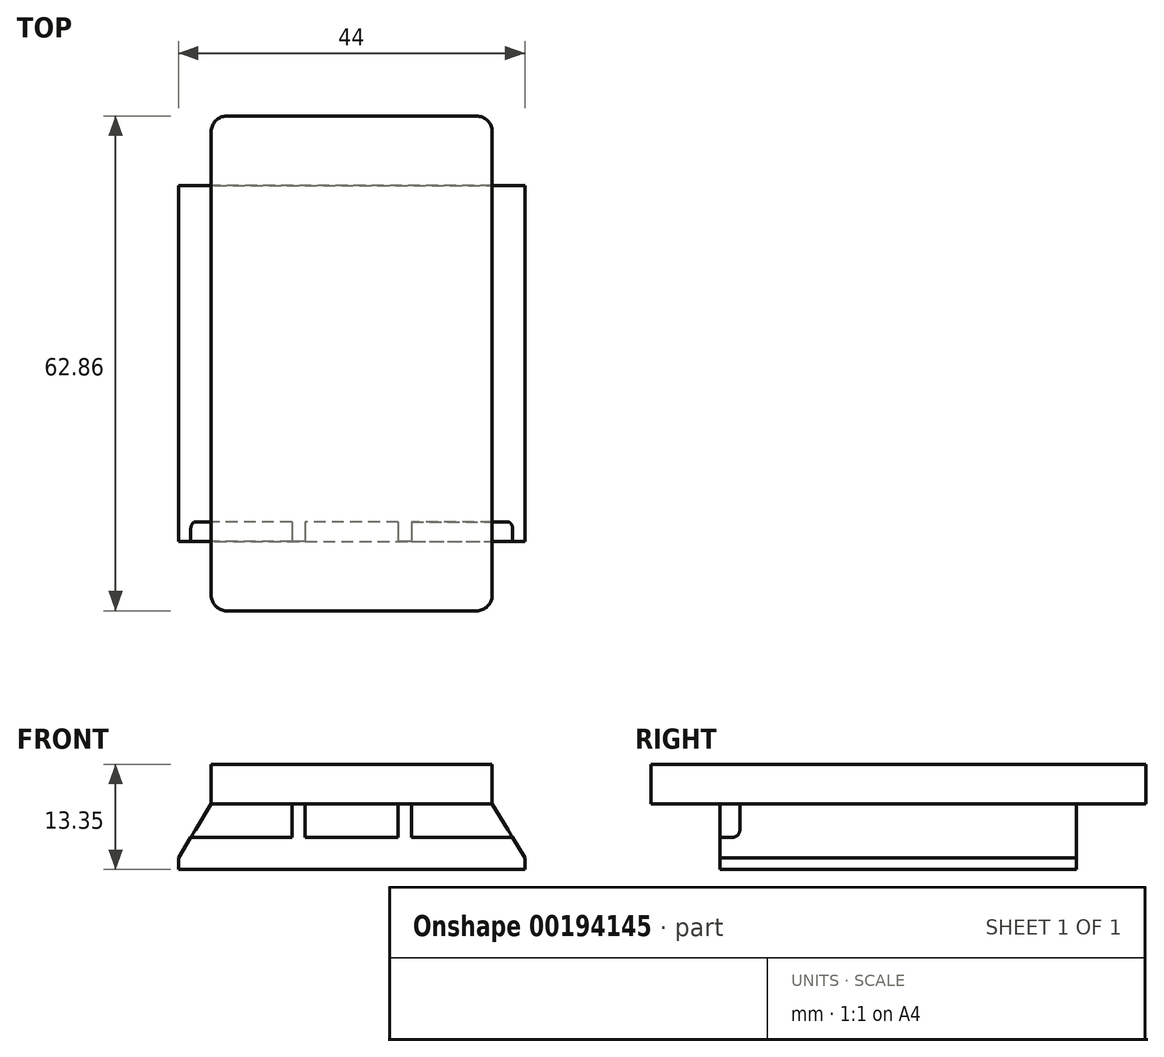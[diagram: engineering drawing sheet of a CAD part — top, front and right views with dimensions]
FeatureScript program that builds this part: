
annotation { "Feature Type Name" : "Feature", "Feature Type Description" : "" }
export const myFeature = defineFeature(function(context is Context, id is Id, definition is map)
    precondition{}
    {
        {
            var Q0;
            Q0=qCreatedBy(makeId("Top.planeOp"),FACE);
            var sketch = newSketch(context, id + "F0", { "sketchPlane" : qUnion([Q0])});
            skLineSegment(sketch, "E0.bottom", {"start": v(15.85, -31.43) * mm, "end": v(-15.85, -31.43) * mm});
            skLineSegment(sketch, "E0.top", {"start": v(15.85, 31.43) * mm, "end": v(-15.85, 31.43) * mm});
            skLineSegment(sketch, "E0.left", {"start": v(17.85, -29.42) * mm, "end": v(17.85, 29.43) * mm});
            skLineSegment(sketch, "E0.right", {"start": v(-17.85, -29.43) * mm, "end": v(-17.85, 29.43) * mm});
            skPoint(sketch, "E0.middle", {"position": v(0, 0) * mm});
            skPoint(sketch, "E1.visualSharp", {"position": v(-17.85, 31.43) * mm});
            skArc(sketch, "E1.filletArc", {"start": v(-15.85, 31.43) * mm, "mid": v(-17.26, 30.84) * mm, "end": v(-17.85, 29.43) * mm});
            skPoint(sketch, "E2.visualSharp", {"position": v(17.85, 31.43) * mm});
            skArc(sketch, "E2.filletArc", {"start": v(17.85, 29.43) * mm, "mid": v(17.26, 30.84) * mm, "end": v(15.85, 31.43) * mm});
            skPoint(sketch, "E3.visualSharp", {"position": v(17.85, -31.43) * mm});
            skArc(sketch, "E3.filletArc", {"start": v(15.85, -31.42) * mm, "mid": v(17.26, -30.84) * mm, "end": v(17.85, -29.42) * mm});
            skPoint(sketch, "E4.visualSharp", {"position": v(-17.85, -31.43) * mm});
            skArc(sketch, "E4.filletArc", {"start": v(-17.85, -29.43) * mm, "mid": v(-17.26, -30.84) * mm, "end": v(-15.85, -31.43) * mm});
            skSolve(sketch);
        }
        {
            var Q0;
            Q0=qSketchRegion(id+"F0",true);
            extrude(context, id + "F1", {"entities" : qUnion([Q0]), "oppositeDirection" : true, "depth" : 5 * mm});
        }
        {
            var Q0;
            Q0=makeQuery(id+"F1.opExtrude","CAP_FACE",FACE,{"disambiguationData":[OSD([sQuery(id+"F0.wireOp",EDGE,"E0.bottom"),sQuery(id+"F0.wireOp",EDGE,"E0.top"),sQuery(id+"F0.wireOp",EDGE,"E0.left"),sQuery(id+"F0.wireOp",EDGE,"E0.right"),sQuery(id+"F0.wireOp",EDGE,"E1.filletArc"),sQuery(id+"F0.wireOp",EDGE,"E2.filletArc"),sQuery(id+"F0.wireOp",EDGE,"E3.filletArc"),sQuery(id+"F0.wireOp",EDGE,"E4.filletArc")])],"isStart":false});
            var sketch = newSketch(context, id + "F2", { "sketchPlane" : qUnion([Q0])});
            skLineSegment(sketch, "E5.bottom", {"start": v(17.85, 22.62) * mm, "end": v(-17.85, 22.62) * mm});
            skLineSegment(sketch, "E5.top", {"start": v(17.85, -22.62) * mm, "end": v(-17.85, -22.62) * mm});
            skLineSegment(sketch, "E5.left", {"start": v(17.85, 22.62) * mm, "end": v(17.85, -22.62) * mm});
            skLineSegment(sketch, "E5.right", {"start": v(-17.85, 22.62) * mm, "end": v(-17.85, -22.62) * mm});
            skPoint(sketch, "E5.middle", {"position": v(0, 0) * mm});
            skSolve(sketch);
        }
        {
            var Q0;
            Q0=makeQuery(id+"F2.imprint","IMPRINT",FACE,{"disambiguationData":[TD([[makeQuery(id+"F2.imprint","IMPRINT",EDGE,{"derivedFrom":sQuery(id+"F2.wireOp",EDGE,"E5.bottom")}),1.0]])]});
            cPlane(context, id + "F3", {"entities" : qUnion([Q0]), "cplaneType" : CPlaneType.OFFSET, "offset" : 6.85 * mm, "width" : 150 * mm, "height" : 150 * mm});
        }
        {
            var Q0;
            Q0=qCreatedBy(id+"F3.planeOp",FACE);
            var sketch = newSketch(context, id + "F4", { "sketchPlane" : qUnion([Q0])});
            skLineSegment(sketch, "E6.bottom", {"start": v(-22, -22.62) * mm, "end": v(22, -22.62) * mm});
            skLineSegment(sketch, "E6.top", {"start": v(-22, 22.62) * mm, "end": v(22, 22.62) * mm});
            skLineSegment(sketch, "E6.left", {"start": v(-22, -22.62) * mm, "end": v(-22, 22.62) * mm});
            skLineSegment(sketch, "E6.right", {"start": v(22, -22.62) * mm, "end": v(22, 22.62) * mm});
            skPoint(sketch, "E6.middle", {"position": v(0, 0) * mm});
            skSolve(sketch);
        }
        {
            var Q1;
            Q1 = qSketchRegion(id + "F2", true);
            var Q2;
            Q2 = qSketchRegion(id + "F4", true);
            loft(context, id + "F5", {"operationType" : NewBodyOperationType.ADD, "sheetProfilesArray" : [{ "sheetProfileEntities" : qUnion([Q1]) }, { "sheetProfileEntities" : qUnion([Q2]) }]});
        }
        {
            var Q0;
            Q0 = qSketchRegion(id + "F4", true);
            extrude(context, id + "F6", {"entities" : qUnion([Q0]), "operationType" : NewBodyOperationType.ADD, "depth" : 1.5 * mm});
        }
        {
            var Q0;
            {var subQ0=sQuery(id+"F4.wireOp",EDGE,"E6.top");Q0=makeQuery(id+"F6.boolean.opBoolean","MERGE",FACE,{"derivedFrom":[makeQuery(id+"F5.opLoft","SWEPT_FACE",FACE,{"disambiguationData":[OSD([sQuery(id+"F0.wireOp",EDGE,"E0.left"),sQuery(id+"F0.wireOp",EDGE,"E0.right"),sQuery(id+"F2.wireOp",EDGE,"E5.bottom"),sQuery(id+"F2.wireOp",EDGE,"E5.left"),sQuery(id+"F2.wireOp",EDGE,"E5.right"),subQ0,sQuery(id+"F4.wireOp",EDGE,"E6.left"),sQuery(id+"F4.wireOp",EDGE,"E6.right")])]}),makeQuery(id+"F6.opExtrude","SWEPT_FACE",FACE,{"disambiguationData":[OSD([subQ0])]})]});}
            var sketch = newSketch(context, id + "F7", { "sketchPlane" : qUnion([Q0])});
            skLineSegment(sketch, "E7", {"start": v(0, -5) * mm, "end": v(-5.9, -5) * mm});
            skLineSegment(sketch, "E8", {"start": v(-5.9, -5) * mm, "end": v(-5.9, -9.3) * mm});
            skLineSegment(sketch, "E9", {"start": v(-5.9, -9.3) * mm, "end": v(0, -9.3) * mm});
            skLineSegment(sketch, "E10", {"start": v(-7.6, -5) * mm, "end": v(-7.6, -9.3) * mm});
            skLineSegment(sketch, "E11", {"start": v(-7.6, -9.3) * mm, "end": v(-20.46, -9.3) * mm});
            skLineSegment(sketch, "E12", {"start": v(-20.46, -9.3) * mm, "end": v(-17.85, -5) * mm});
            skLineSegment(sketch, "E13", {"start": v(-17.85, -5) * mm, "end": v(-7.6, -5) * mm});
            skLineSegment(sketch, "E14.MirrorCS", {"start": v(5.9, -5) * mm, "end": v(5.9, -9.3) * mm});
            skLineSegment(sketch, "E15.MirrorCS", {"start": v(0, -5) * mm, "end": v(5.9, -5) * mm});
            skLineSegment(sketch, "E16.MirrorCS", {"start": v(5.9, -9.3) * mm, "end": v(0, -9.3) * mm});
            skLineSegment(sketch, "E17.MirrorCS", {"start": v(7.6, -5) * mm, "end": v(7.6, -9.3) * mm});
            skLineSegment(sketch, "E18.MirrorCS", {"start": v(7.6, -9.3) * mm, "end": v(20.46, -9.3) * mm});
            skLineSegment(sketch, "E19.MirrorCS", {"start": v(17.85, -5) * mm, "end": v(7.6, -5) * mm});
            skLineSegment(sketch, "E20.MirrorCS", {"start": v(20.46, -9.3) * mm, "end": v(17.85, -5) * mm});
            skSolve(sketch);
        }
        {
            var Q0;
            Q0 = qSketchRegion(id + "F7", true);
            extrude(context, id + "F8", {"entities" : qUnion([Q0]), "operationType" : NewBodyOperationType.REMOVE, "oppositeDirection" : true, "depth" : 2.5 * mm});
        }
        {
            var Q0;
            Q0=makeQuery(id+"F8.boolean.opBoolean","COPY",EDGE,{"derivedFrom":makeQuery(id+"F8.opExtrude","CAP_EDGE",EDGE,{"disambiguationData":[OSD([sQuery(id+"F7.wireOp",EDGE,"E11")])],"isStart":false})});
            var Q1;
            Q1=makeQuery(id+"F8.boolean.opBoolean","COPY",EDGE,{"derivedFrom":makeQuery(id+"F8.opExtrude","CAP_EDGE",EDGE,{"disambiguationData":[OSD([sQuery(id+"F7.wireOp",EDGE,"E9"),sQuery(id+"F7.wireOp",EDGE,"E16.MirrorCS")])],"isStart":false})});
            var Q2;
            Q2=makeQuery(id+"F8.boolean.opBoolean","COPY",EDGE,{"derivedFrom":makeQuery(id+"F8.opExtrude","CAP_EDGE",EDGE,{"disambiguationData":[OSD([sQuery(id+"F7.wireOp",EDGE,"E18.MirrorCS")])],"isStart":false})});
            fillet(context, id + "F9", {"entities" : qUnion([Q0, Q1, Q2]), "radius" : 1 * mm, "tangentPropagation" : true, "allowEdgeOverflow" : false});
        }
    });
